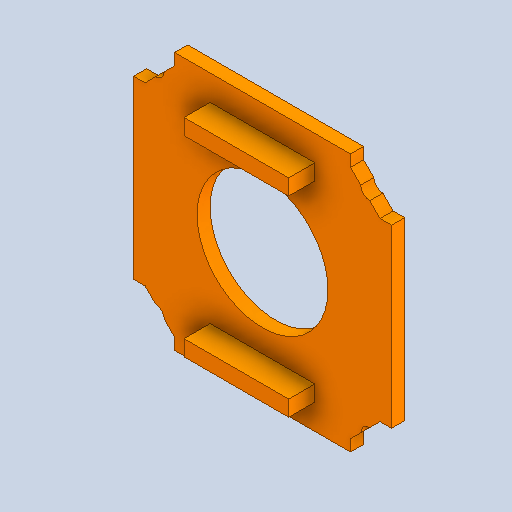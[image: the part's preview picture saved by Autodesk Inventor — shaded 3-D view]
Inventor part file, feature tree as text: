
AUTODESK INVENTOR PART (.ipt)
format: ipt  version: 2023 (Build 270158030, 158C)  size: 219,648 bytes
history: native  units: mm
features: other x4, sketch x3, extrude x3, plane x2, reference x2, pattern_circular x1
ambient origin geometry x8: Origin, YZ Plane, XZ Plane, XY Plane, X Axis, Y Axis, Z Axis, Center Point
bodies: Solid1 (feature_tree)
feature tree (15):
  sketch  "Sketch1"  dims[d0=0.25mm d1=25.0mm]
  plane  "Work Plane1"
  extrude  "Extrusion1"  Depth=25.0mm
  extrude  "Extrusion2"  Depth=3.0mm
  sketch  "Sketch3"  dims[d4=20.0mm d5=3.0mm d6=20.0mm d7=3.0mm d8=20.0mm d9=3.0mm d10=2.5mm d11=0.0mm d12=0.25mm d13=25.0mm d14=20.0mm d15=3.0mm d16=20.0mm d17=3.0mm d18=20.0mm d19=3.0mm d20=20.0mm d21=3.0mm d22=5.0mm d23=0.0mm d24=10.0mm d25=0.0mm d26=20.0mm d27=90.0deg]
  plane  "Work Plane2"
  extrude  "Extrusion3"  Depth=3.0mm
  pattern_circular  "Circular Pattern1"  Count=2  [1 undecoded]
  reference  "Reference1"
  sketch  "Sketch2"  dims[d2=20.0mm d3=3.0mm]
  reference  "Reference3"
  other  "Cube V1-2.iam"
  other  "Cube 1x1 Bottom V1-2:1"
  other  "Cube 1x1 V2.iam"
  other  "Cube 1x1 Bottom V2:1"
note: 1 required parameter value undecoded (feature->parameter linkage not recoverable at this tier; creation-order binding heuristic only, values carry confidence <= 0.55)
